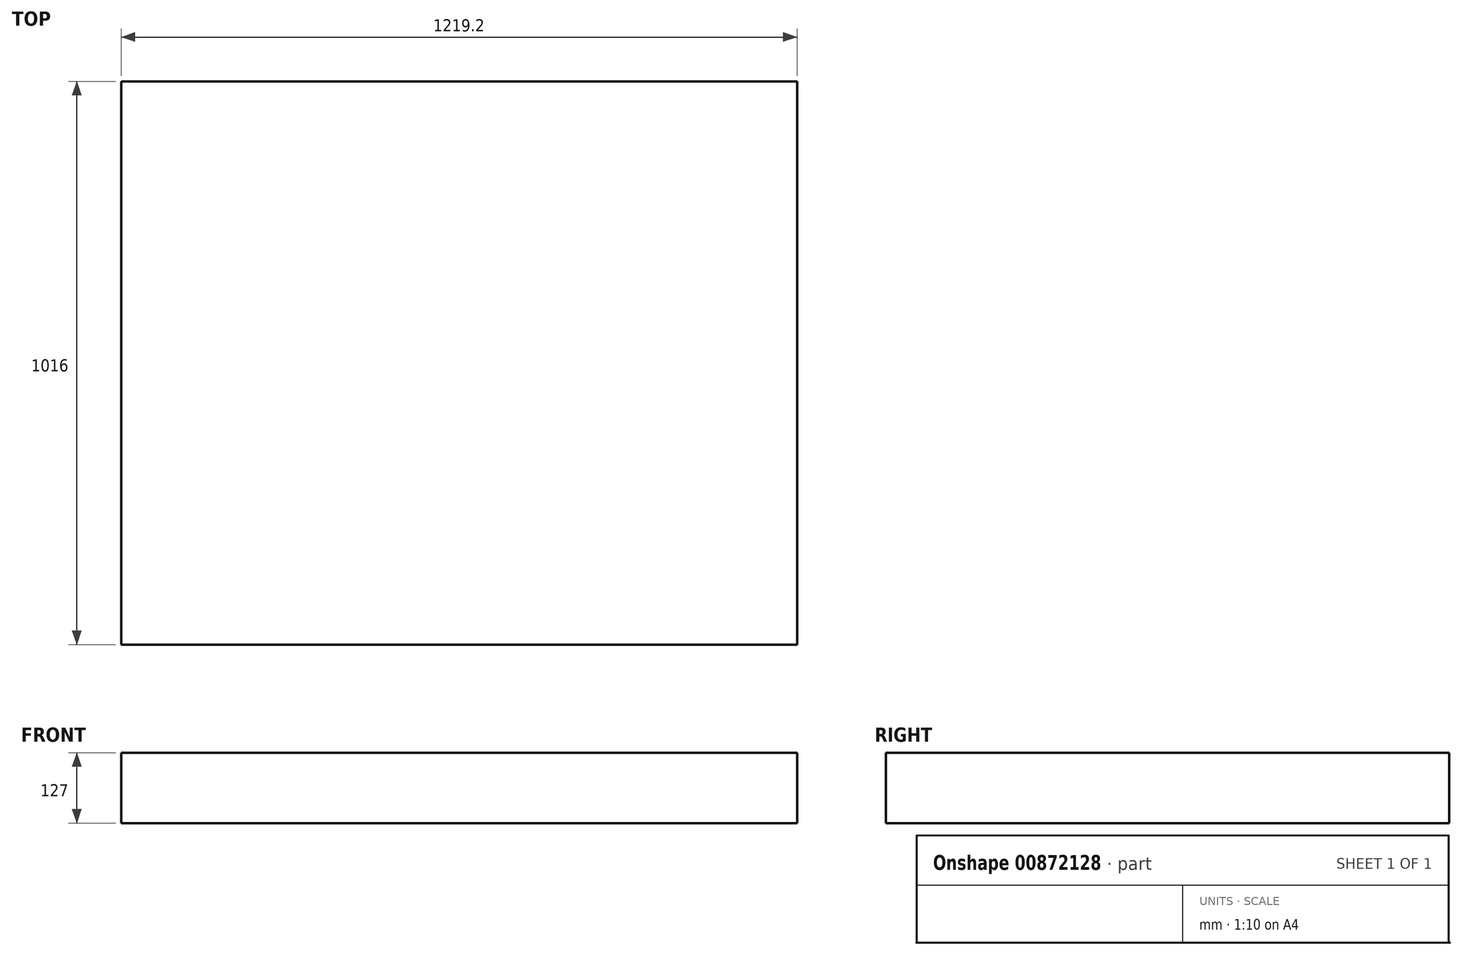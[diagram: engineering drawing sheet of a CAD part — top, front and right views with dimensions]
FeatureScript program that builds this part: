
annotation { "Feature Type Name" : "Feature", "Feature Type Description" : "" }
export const myFeature = defineFeature(function(context is Context, id is Id, definition is map)
    precondition{}
    {
        {
            var Q0;
            Q0=qCreatedBy(makeId("Front.planeOp"),FACE);
            var sketch = newSketch(context, id + "F0", { "sketchPlane" : qUnion([Q0])});
            skLineSegment(sketch, "E0.bottom", {"start": v(0, 0) * mm, "end": v(1219.2, 0) * mm});
            skLineSegment(sketch, "E0.top", {"start": v(0, 127) * mm, "end": v(1219.2, 127) * mm});
            skLineSegment(sketch, "E0.left", {"start": v(0, 0) * mm, "end": v(0, 127) * mm});
            skLineSegment(sketch, "E0.right", {"start": v(1219.2, 0) * mm, "end": v(1219.2, 127) * mm});
            skSolve(sketch);
        }
        {
            var Q0;
            Q0 = qSketchRegion(id + "F0", true);
            extrude(context, id + "F1", {"entities" : qUnion([Q0]), "depth" : 1016 * mm, "offsetDistance" : 25.4 * mm});
        }
    });
